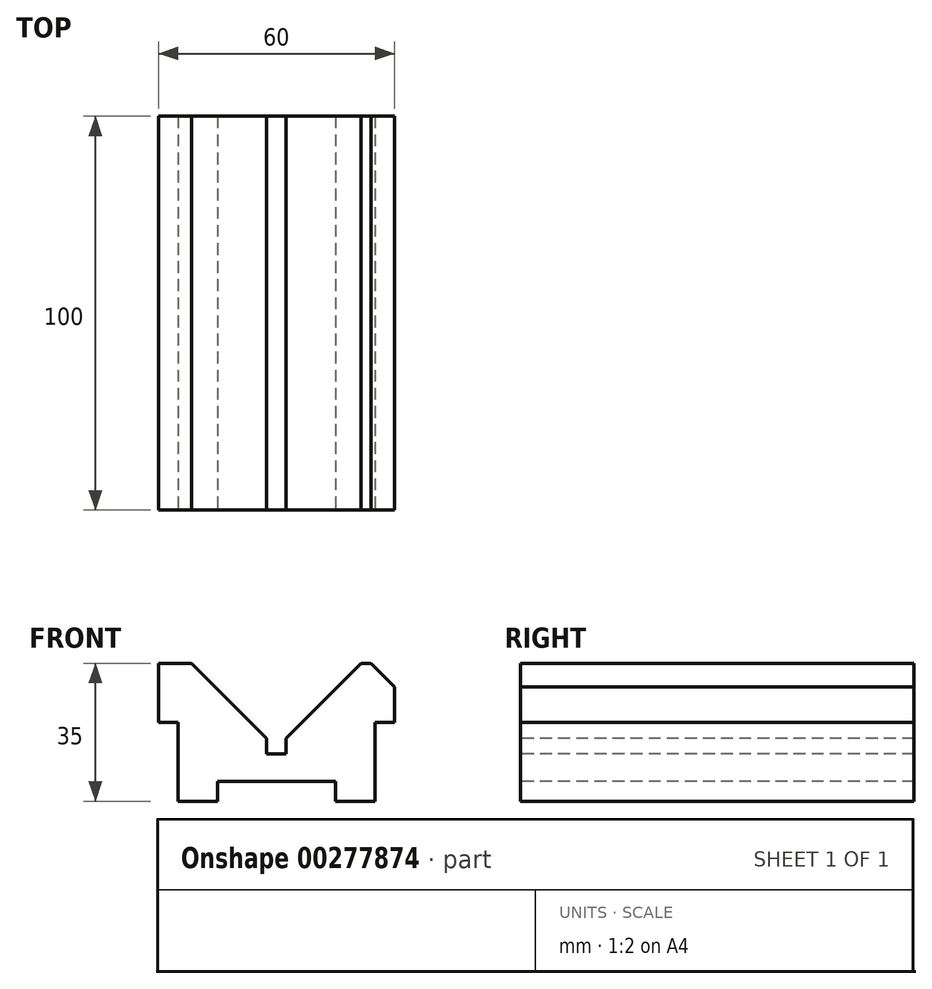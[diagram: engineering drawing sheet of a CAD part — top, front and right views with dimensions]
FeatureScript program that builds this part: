
annotation { "Feature Type Name" : "Feature", "Feature Type Description" : "" }
export const myFeature = defineFeature(function(context is Context, id is Id, definition is map)
    precondition{}
    {
        {
            var Q0;
            Q0=qCreatedBy(makeId("Right.planeOp"),FACE);
            var sketch = newSketch(context, id + "F0", { "sketchPlane" : qUnion([Q0])});
            skLineSegment(sketch, "E0", {"start": v(-50, 17.5) * mm, "end": v(-50, -17.5) * mm});
            skLineSegment(sketch, "E1", {"start": v(-50, 17.5) * mm, "end": v(50, 17.5) * mm});
            skLineSegment(sketch, "E2", {"start": v(50, 17.5) * mm, "end": v(50, -17.5) * mm});
            skLineSegment(sketch, "E3", {"start": v(50, -17.5) * mm, "end": v(-50, -17.5) * mm});
            skSolve(sketch);
        }
        {
            var Q0;
            Q0=makeQuery(id+"F0.imprint","IMPRINT",FACE,{"disambiguationData":[TD([[makeQuery(id+"F0.imprint","IMPRINT",EDGE,{"derivedFrom":sQuery(id+"F0.wireOp",EDGE,"E0")}),1.0]])]});
            extrude(context, id + "F1", {"entities" : qUnion([Q0]), "endBound" : BoundingType.SYMMETRIC, "depth" : 60 * mm});
        }
        {
            var Q0;
            Q0=makeQuery(id+"F1.opExtrude","SWEPT_FACE",FACE,{"disambiguationData":[OSD([sQuery(id+"F0.wireOp",EDGE,"E0")])]});
            var sketch = newSketch(context, id + "F2", { "sketchPlane" : qUnion([Q0])});
            skLineSegment(sketch, "E4", {"start": v(-25, -17.5) * mm, "end": v(-25, 2.5) * mm});
            skLineSegment(sketch, "E5", {"start": v(-25, 2.5) * mm, "end": v(-30, 2.5) * mm});
            skLineSegment(sketch, "E6.MirrorCS", {"start": v(25, 2.5) * mm, "end": v(30, 2.5) * mm});
            skLineSegment(sketch, "E7.MirrorCS", {"start": v(25, -17.5) * mm, "end": v(25, 2.5) * mm});
            skLineSegment(sketch, "E8", {"start": v(-15, -17.5) * mm, "end": v(-15, -12.5) * mm});
            skLineSegment(sketch, "E9", {"start": v(-15, -12.5) * mm, "end": v(15, -12.5) * mm});
            skLineSegment(sketch, "E10", {"start": v(15, -12.5) * mm, "end": v(15, -17.5) * mm});
            skLineSegment(sketch, "E11", {"start": v(-30, -17.5) * mm, "end": v(-30, 2.5) * mm});
            skLineSegment(sketch, "E12", {"start": v(-30, -17.5) * mm, "end": v(-25, -17.5) * mm});
            skLineSegment(sketch, "E13", {"start": v(-15, -17.5) * mm, "end": v(15, -17.5) * mm});
            skLineSegment(sketch, "E14.MirrorCS", {"start": v(30, -17.5) * mm, "end": v(25, -17.5) * mm});
            skLineSegment(sketch, "E15.MirrorCS", {"start": v(30, -17.5) * mm, "end": v(30, 2.5) * mm});
            skSolve(sketch);
        }
        {
            var Q0;
            Q0=makeQuery(id+"F2.imprint","IMPRINT",FACE,{"disambiguationData":[TD([[makeQuery(id+"F2.imprint","IMPRINT",EDGE,{"derivedFrom":sQuery(id+"F2.wireOp",EDGE,"E4")}),1.0]])]});
            var Q1;
            Q1=makeQuery(id+"F2.imprint","IMPRINT",FACE,{"disambiguationData":[TD([[makeQuery(id+"F2.imprint","IMPRINT",EDGE,{"derivedFrom":sQuery(id+"F2.wireOp",EDGE,"E8")}),-1.0]])]});
            var Q2;
            Q2=makeQuery(id+"F2.imprint","IMPRINT",FACE,{"disambiguationData":[TD([[makeQuery(id+"F2.imprint","IMPRINT",EDGE,{"derivedFrom":sQuery(id+"F2.wireOp",EDGE,"E6.MirrorCS")}),-1.0]])]});
            extrude(context, id + "F3", {"entities" : qUnion([Q0, Q1, Q2]), "operationType" : NewBodyOperationType.REMOVE, "oppositeDirection" : true, "depth" : 100 * mm});
        }
        {
            var Q0;
            Q0=qCreatedBy(makeId("Front.planeOp"),FACE);
            var sketch = newSketch(context, id + "F4", { "sketchPlane" : qUnion([Q0])});
            skLineSegment(sketch, "E16", {"start": v(-24, 17.5) * mm, "end": v(-30, 17.5) * mm});
            skLineSegment(sketch, "E17", {"start": v(-30, 17.5) * mm, "end": v(-30, 11.5) * mm});
            skLineSegment(sketch, "E18", {"start": v(-30, 11.5) * mm, "end": v(-24, 17.5) * mm});
            skLineSegment(sketch, "E19.MirrorCS", {"start": v(30, 17.5) * mm, "end": v(30, 11.5) * mm});
            skLineSegment(sketch, "E20.MirrorCS", {"start": v(24, 17.5) * mm, "end": v(30, 17.5) * mm});
            skLineSegment(sketch, "E21.MirrorCS", {"start": v(30, 11.5) * mm, "end": v(24, 17.5) * mm});
            skLineSegment(sketch, "E22", {"start": v(-24, 17.5) * mm, "end": v(-30, 11.5) * mm});
            skLineSegment(sketch, "E23", {"start": v(-30, 11.5) * mm, "end": v(-30, 17.5) * mm});
            skLineSegment(sketch, "E24", {"start": v(-30, 17.5) * mm, "end": v(-24, 17.5) * mm});
            skLineSegment(sketch, "E25.MirrorCS", {"start": v(24, 17.5) * mm, "end": v(30, 11.5) * mm});
            skSolve(sketch);
        }
        {
            var Q0;
            Q0=makeQuery(id+"F4.imprint","IMPRINT",FACE,{"disambiguationData":[TD([[makeQuery(id+"F4.imprint","IMPRINT",EDGE,{"derivedFrom":sQuery(id+"F4.wireOp",EDGE,"E19.MirrorCS")}),-1.0]])]});
            var Q1;
            Q1=makeQuery(id+"F4.imprint","IMPRINT",FACE,{"disambiguationData":[TD([[makeQuery(id+"F4.imprint","IMPRINT",EDGE,{"derivedFrom":sQuery(id+"F4.wireOp",EDGE,"E22")}),-1.0]])]});
            extrude(context, id + "F5", {"entities" : qUnion([Q0, Q1]), "operationType" : NewBodyOperationType.REMOVE, "oppositeDirection" : true, "depth" : 100 * mm, "hasSecondDirection" : true, "secondDirectionOppositeDirection" : false, "secondDirectionDepth" : 74.2 * mm});
        }
        {
            var Q0;
            Q0=qCreatedBy(makeId("Front.planeOp"),FACE);
            var sketch = newSketch(context, id + "F6", { "sketchPlane" : qUnion([Q0])});
            skLineSegment(sketch, "E26", {"start": v(2.5, -1.5) * mm, "end": v(2.5, -5.5) * mm});
            skLineSegment(sketch, "E27", {"start": v(2.5, -5.5) * mm, "end": v(-2.5, -5.5) * mm});
            skLineSegment(sketch, "E28", {"start": v(-2.5, -5.5) * mm, "end": v(-2.5, -1.5) * mm});
            skLineSegment(sketch, "E29", {"start": v(-2.5, -1.5) * mm, "end": v(-21.5, 17.5) * mm});
            skLineSegment(sketch, "E30", {"start": v(2.5, -1.5) * mm, "end": v(21.5, 17.5) * mm});
            skLineSegment(sketch, "E31", {"start": v(-21.5, 17.5) * mm, "end": v(21.5, 17.5) * mm});
            skSolve(sketch);
        }
        {
            var Q0;
            Q0 = qSketchRegion(id + "F6", true);
            extrude(context, id + "F7", {"entities" : qUnion([Q0]), "operationType" : NewBodyOperationType.REMOVE, "oppositeDirection" : true, "depth" : 100 * mm, "hasSecondDirection" : true, "secondDirectionOppositeDirection" : false, "secondDirectionDepth" : 100.7 * mm});
        }
    });
